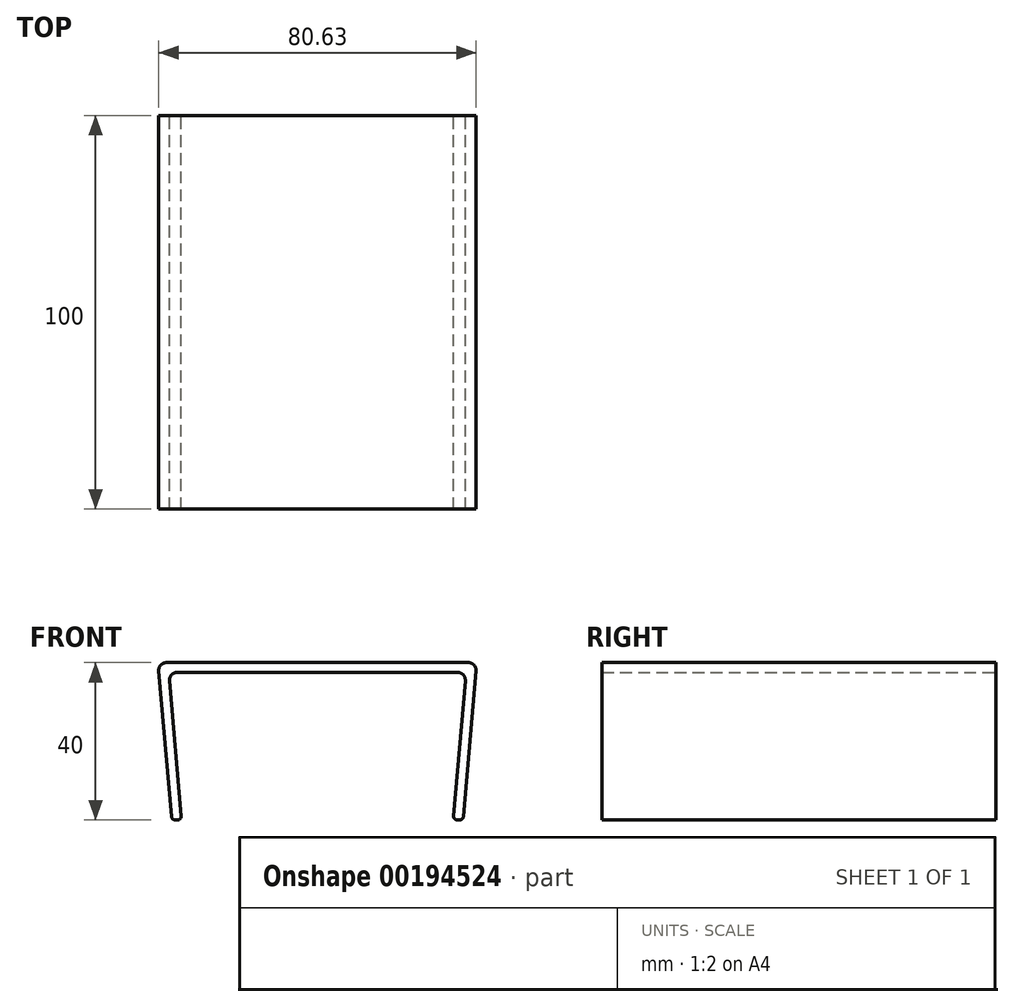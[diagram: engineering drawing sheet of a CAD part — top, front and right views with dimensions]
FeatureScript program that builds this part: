
annotation { "Feature Type Name" : "Feature", "Feature Type Description" : "" }
export const myFeature = defineFeature(function(context is Context, id is Id, definition is map)
    precondition{}
    {
        {
            var Q0;
            Q0=qCreatedBy(makeId("Front.planeOp"),FACE);
            var sketch = newSketch(context, id + "F0", { "sketchPlane" : qUnion([Q0])});
            skLineSegment(sketch, "E0.bottom", {"start": v(44.1, 16.74) * mm, "end": v(-32.53, 16.74) * mm});
            skPoint(sketch, "E0.middle", {"position": v(0, 0) * mm});
            skLineSegment(sketch, "E1", {"start": v(-34.52, 14.56) * mm, "end": v(-31.3, -22.35) * mm});
            skLineSegment(sketch, "E2", {"start": v(46.1, 14.56) * mm, "end": v(42.87, -22.35) * mm});
            skLineSegment(sketch, "E3.0", {"start": v(-31.8, 12.06) * mm, "end": v(-28.8, -22.17) * mm});
            skLineSegment(sketch, "E3.1", {"start": v(41.37, 14.24) * mm, "end": v(-29.8, 14.24) * mm});
            skLineSegment(sketch, "E3.2", {"start": v(43.37, 12.06) * mm, "end": v(40.37, -22.17) * mm});
            skLineSegment(sketch, "E4", {"start": v(-30.3, -23.26) * mm, "end": v(-29.8, -23.26) * mm});
            skLineSegment(sketch, "E5.trimOffspring", {"start": v(41.37, -23.26) * mm, "end": v(41.87, -23.26) * mm});
            skPoint(sketch, "E6.visualSharp", {"position": v(-34.71, 16.74) * mm});
            skArc(sketch, "E6.filletArc", {"start": v(-32.53, 16.74) * mm, "mid": v(-34, 16.09) * mm, "end": v(-34.52, 14.56) * mm});
            skPoint(sketch, "E7.visualSharp", {"position": v(-31.99, 14.24) * mm});
            skArc(sketch, "E7.filletArc", {"start": v(-29.8, 14.24) * mm, "mid": v(-31.28, 13.59) * mm, "end": v(-31.8, 12.06) * mm});
            skPoint(sketch, "E8.visualSharp", {"position": v(46.29, 16.74) * mm});
            skArc(sketch, "E8.filletArc", {"start": v(46.1, 14.56) * mm, "mid": v(45.58, 16.09) * mm, "end": v(44.1, 16.74) * mm});
            skPoint(sketch, "E9.visualSharp", {"position": v(43.56, 14.24) * mm});
            skArc(sketch, "E9.filletArc", {"start": v(43.37, 12.06) * mm, "mid": v(42.85, 13.59) * mm, "end": v(41.37, 14.24) * mm});
            skPoint(sketch, "E10.visualSharp", {"position": v(-31.22, -23.26) * mm});
            skArc(sketch, "E10.filletArc", {"start": v(-31.3, -22.35) * mm, "mid": v(-30.97, -23) * mm, "end": v(-30.3, -23.26) * mm});
            skPoint(sketch, "E11.visualSharp", {"position": v(-28.7, -23.26) * mm});
            skArc(sketch, "E11.filletArc", {"start": v(-29.8, -23.26) * mm, "mid": v(-29.06, -22.94) * mm, "end": v(-28.8, -22.17) * mm});
            skPoint(sketch, "E12.visualSharp", {"position": v(42.79, -23.26) * mm});
            skArc(sketch, "E12.filletArc", {"start": v(41.87, -23.26) * mm, "mid": v(42.55, -23) * mm, "end": v(42.87, -22.35) * mm});
            skPoint(sketch, "E13.visualSharp", {"position": v(40.28, -23.26) * mm});
            skArc(sketch, "E13.filletArc", {"start": v(40.37, -22.17) * mm, "mid": v(40.63, -22.94) * mm, "end": v(41.37, -23.26) * mm});
            skSolve(sketch);
        }
        {
            var Q0;
            Q0=makeQuery(id+"F0.imprint","IMPRINT",FACE,{"disambiguationData":[TD([[makeQuery(id+"F0.imprint","IMPRINT",EDGE,{"derivedFrom":sQuery(id+"F0.wireOp",EDGE,"E0.bottom")}),1.0]])]});
            extrude(context, id + "F1", {"entities" : qUnion([Q0]), "depth" : 100 * mm});
        }
    });
